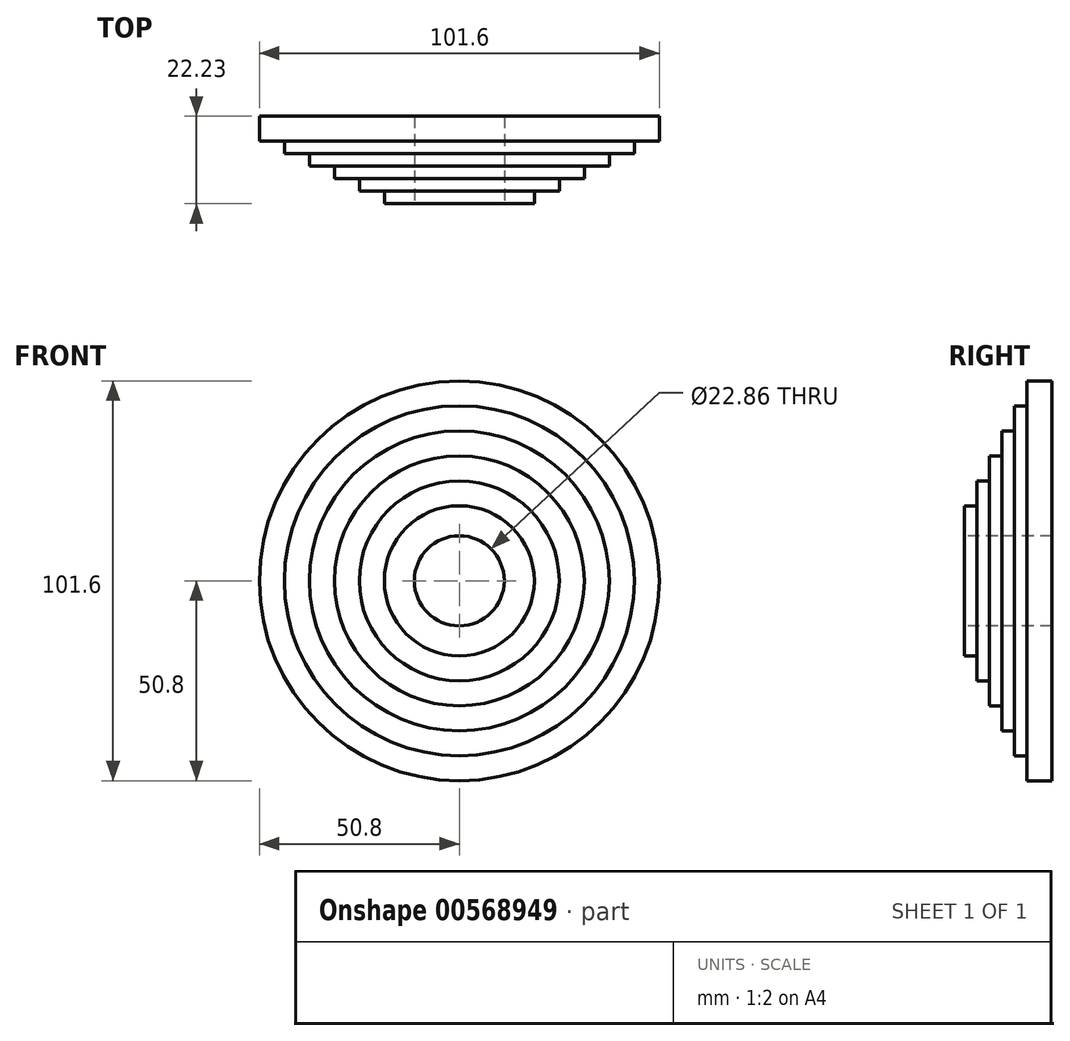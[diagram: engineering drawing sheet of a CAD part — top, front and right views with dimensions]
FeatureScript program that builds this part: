
annotation { "Feature Type Name" : "Feature", "Feature Type Description" : "" }
export const myFeature = defineFeature(function(context is Context, id is Id, definition is map)
    precondition{}
    {
        {
            var Q0;
            Q0=qCreatedBy(makeId("Front.planeOp"),FACE);
            var sketch = newSketch(context, id + "F0", { "sketchPlane" : qUnion([Q0])});
            skCircle(sketch, "E0", {"center": v(0, 0) * mm, "radius": 50.8 * mm});
            skSolve(sketch);
        }
        {
            var Q0;
            Q0 = qSketchRegion(id + "F0", true);
            extrude(context, id + "F1", {"entities" : qUnion([Q0]), "depth" : 3.17 * mm, "offsetDistance" : 25.4 * mm});
        }
        {
            var Q0;
            Q0=makeQuery(id+"F1.opExtrude","CAP_FACE",FACE,{"disambiguationData":[OSD([sQuery(id+"F0.wireOp",EDGE,"E0")])],"isStart":false});
            var sketch = newSketch(context, id + "F2", { "sketchPlane" : qUnion([Q0])});
            skCircle(sketch, "E1", {"center": v(0, 0) * mm, "radius": 50.8 * mm});
            skSolve(sketch);
        }
        {
            var Q0;
            Q0 = qSketchRegion(id + "F2", true);
            extrude(context, id + "F3", {"entities" : qUnion([Q0]), "operationType" : NewBodyOperationType.ADD, "depth" : 3.17 * mm, "offsetDistance" : 25.4 * mm});
        }
        {
            var Q0;
            Q0=makeQuery(id+"F3.opExtrude","CAP_FACE",FACE,{"disambiguationData":[OSD([sQuery(id+"F2.wireOp",EDGE,"E1")])],"isStart":false});
            var sketch = newSketch(context, id + "F4", { "sketchPlane" : qUnion([Q0])});
            skCircle(sketch, "E2", {"center": v(0, 0) * mm, "radius": 44.45 * mm});
            skSolve(sketch);
        }
        {
            var Q0;
            Q0 = qSketchRegion(id + "F4", true);
            extrude(context, id + "F5", {"entities" : qUnion([Q0]), "operationType" : NewBodyOperationType.ADD, "depth" : 3.17 * mm, "offsetDistance" : 25.4 * mm});
        }
        {
            var Q0;
            Q0=makeQuery(id+"F5.opExtrude","CAP_FACE",FACE,{"disambiguationData":[OSD([sQuery(id+"F4.wireOp",EDGE,"E2")])],"isStart":false});
            var sketch = newSketch(context, id + "F6", { "sketchPlane" : qUnion([Q0])});
            skCircle(sketch, "E3", {"center": v(0, 0) * mm, "radius": 38.1 * mm});
            skSolve(sketch);
        }
        {
            var Q0;
            Q0 = qSketchRegion(id + "F6", true);
            extrude(context, id + "F7", {"entities" : qUnion([Q0]), "operationType" : NewBodyOperationType.ADD, "depth" : 3.17 * mm, "offsetDistance" : 25.4 * mm});
        }
        {
            var Q0;
            Q0=makeQuery(id+"F7.opExtrude","CAP_FACE",FACE,{"disambiguationData":[OSD([sQuery(id+"F6.wireOp",EDGE,"E3")])],"isStart":false});
            var sketch = newSketch(context, id + "F8", { "sketchPlane" : qUnion([Q0])});
            skCircle(sketch, "E4", {"center": v(0, 0) * mm, "radius": 31.75 * mm});
            skSolve(sketch);
        }
        {
            var Q0;
            Q0 = qSketchRegion(id + "F8", true);
            extrude(context, id + "F9", {"entities" : qUnion([Q0]), "operationType" : NewBodyOperationType.ADD, "depth" : 3.17 * mm, "offsetDistance" : 25.4 * mm});
        }
        {
            var Q0;
            Q0=makeQuery(id+"F9.opExtrude","CAP_FACE",FACE,{"disambiguationData":[OSD([sQuery(id+"F8.wireOp",EDGE,"E4")])],"isStart":false});
            var sketch = newSketch(context, id + "F10", { "sketchPlane" : qUnion([Q0])});
            skCircle(sketch, "E5", {"center": v(0, 0) * mm, "radius": 25.4 * mm});
            skSolve(sketch);
        }
        {
            var Q0;
            Q0 = qSketchRegion(id + "F10", true);
            extrude(context, id + "F11", {"entities" : qUnion([Q0]), "operationType" : NewBodyOperationType.ADD, "depth" : 3.17 * mm, "offsetDistance" : 25.4 * mm});
        }
        {
            var Q0;
            Q0=makeQuery(id+"F11.opExtrude","CAP_FACE",FACE,{"disambiguationData":[OSD([sQuery(id+"F10.wireOp",EDGE,"E5")])],"isStart":false});
            var sketch = newSketch(context, id + "F12", { "sketchPlane" : qUnion([Q0])});
            skCircle(sketch, "E6", {"center": v(0, 0) * mm, "radius": 19.05 * mm});
            skSolve(sketch);
        }
        {
            var Q0;
            Q0 = qSketchRegion(id + "F12", true);
            extrude(context, id + "F13", {"entities" : qUnion([Q0]), "operationType" : NewBodyOperationType.ADD, "depth" : 3.17 * mm, "offsetDistance" : 25.4 * mm});
        }
        {
            var Q0;
            Q0=makeQuery(id+"F13.opExtrude","CAP_FACE",FACE,{"disambiguationData":[OSD([sQuery(id+"F12.wireOp",EDGE,"E6")])],"isStart":false});
            var sketch = newSketch(context, id + "F14", { "sketchPlane" : qUnion([Q0])});
            skCircle(sketch, "E7", {"center": v(0, 0) * mm, "radius": 11.43 * mm});
            skSolve(sketch);
        }
        {
            var Q0;
            Q0 = qSketchRegion(id + "F14", true);
            extrude(context, id + "F15", {"entities" : qUnion([Q0]), "operationType" : NewBodyOperationType.REMOVE, "oppositeDirection" : true, "depth" : 22.22 * mm, "offsetDistance" : 25.4 * mm});
        }
    });
